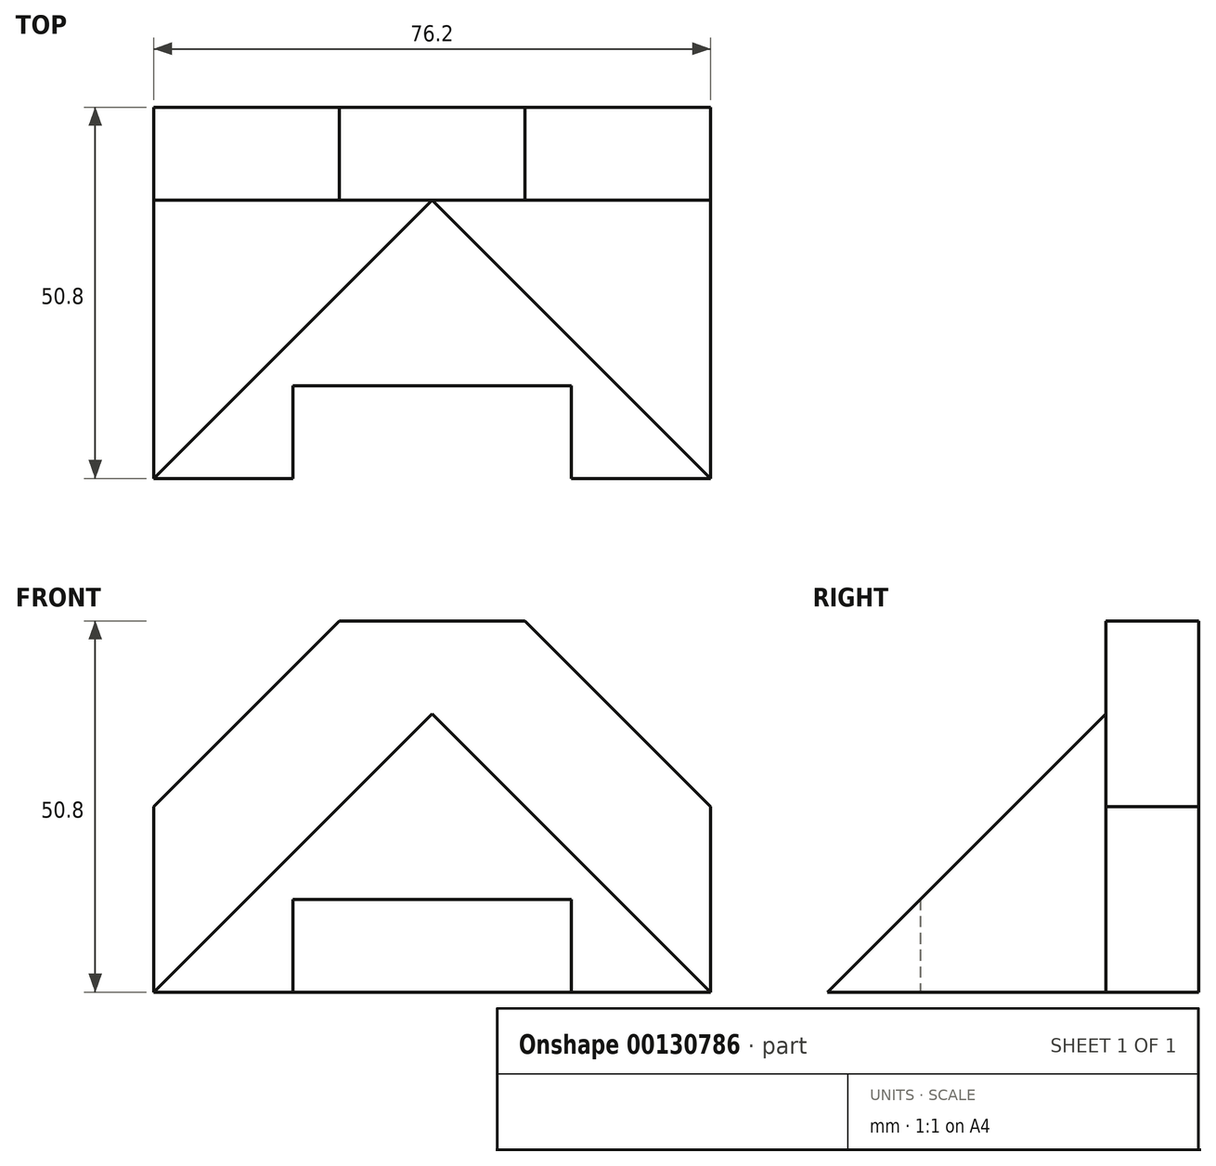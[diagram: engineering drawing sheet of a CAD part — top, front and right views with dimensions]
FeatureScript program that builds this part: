
annotation { "Feature Type Name" : "Feature", "Feature Type Description" : "" }
export const myFeature = defineFeature(function(context is Context, id is Id, definition is map)
    precondition{}
    {
        {
            var Q0;
            Q0=qCreatedBy(makeId("Front.planeOp"),FACE);
            var sketch = newSketch(context, id + "F0", { "sketchPlane" : qUnion([Q0])});
            skLineSegment(sketch, "E0", {"start": v(0, 0) * mm, "end": v(0, 25.4) * mm});
            skLineSegment(sketch, "E1", {"start": v(0, 25.4) * mm, "end": v(25.4, 50.8) * mm});
            skLineSegment(sketch, "E2", {"start": v(25.4, 50.8) * mm, "end": v(50.8, 50.8) * mm});
            skLineSegment(sketch, "E3", {"start": v(50.8, 50.8) * mm, "end": v(76.2, 25.4) * mm});
            skLineSegment(sketch, "E4", {"start": v(76.2, 25.4) * mm, "end": v(76.2, 0) * mm});
            skLineSegment(sketch, "E5", {"start": v(76.2, 0) * mm, "end": v(0, 0) * mm});
            skSolve(sketch);
        }
        {
            var Q0;
            Q0 = qSketchRegion(id + "F0", true);
            extrude(context, id + "F1", {"entities" : qUnion([Q0]), "depth" : 12.7 * mm});
        }
        {
            var Q0;
            Q0=makeQuery(id+"F1.opExtrude","CAP_FACE",FACE,{"disambiguationData":[OSD([sQuery(id+"F0.wireOp",EDGE,"E0"),sQuery(id+"F0.wireOp",EDGE,"E1"),sQuery(id+"F0.wireOp",EDGE,"E2"),sQuery(id+"F0.wireOp",EDGE,"E3"),sQuery(id+"F0.wireOp",EDGE,"E4"),sQuery(id+"F0.wireOp",EDGE,"E5")])],"isStart":false});
            var sketch = newSketch(context, id + "F2", { "sketchPlane" : qUnion([Q0])});
            skLineSegment(sketch, "E6", {"start": v(0, 0) * mm, "end": v(38.1, 38.1) * mm});
            skLineSegment(sketch, "E7", {"start": v(38.1, 38.1) * mm, "end": v(76.2, 0) * mm});
            skLineSegment(sketch, "E8", {"start": v(76.2, 0) * mm, "end": v(0, 0) * mm});
            skSolve(sketch);
        }
        {
            var Q0;
            Q0=makeQuery(id+"F2.imprint","IMPRINT",FACE,{"disambiguationData":[TD([[makeQuery(id+"F2.imprint","IMPRINT",EDGE,{"derivedFrom":sQuery(id+"F2.wireOp",EDGE,"E6")}),-1.0]])]});
            extrude(context, id + "F3", {"entities" : qUnion([Q0]), "operationType" : NewBodyOperationType.ADD, "depth" : 38.1 * mm});
        }
        {
            var Q0;
            Q0=makeQuery(id+"F3.opExtrude","CAP_FACE",FACE,{"disambiguationData":[OSD([sQuery(id+"F2.wireOp",EDGE,"E6"),sQuery(id+"F2.wireOp",EDGE,"E7"),sQuery(id+"F2.wireOp",EDGE,"E8")])],"isStart":false});
            var sketch = newSketch(context, id + "F4", { "sketchPlane" : qUnion([Q0])});
            skLineSegment(sketch, "E9.bottom", {"start": v(19.05, 12.7) * mm, "end": v(57.15, 12.7) * mm});
            skLineSegment(sketch, "E9.top", {"start": v(19.05, 0) * mm, "end": v(57.15, 0) * mm});
            skLineSegment(sketch, "E9.left", {"start": v(19.05, 12.7) * mm, "end": v(19.05, 0) * mm});
            skLineSegment(sketch, "E9.right", {"start": v(57.15, 12.7) * mm, "end": v(57.15, 0) * mm});
            skSolve(sketch);
        }
        {
            var Q0;
            Q0=makeQuery(id+"F4.imprint","IMPRINT",FACE,{"disambiguationData":[TD([[makeQuery(id+"F4.imprint","IMPRINT",EDGE,{"derivedFrom":sQuery(id+"F4.wireOp",EDGE,"E9.bottom")}),-1.0]])]});
            extrude(context, id + "F5", {"entities" : qUnion([Q0]), "operationType" : NewBodyOperationType.REMOVE, "oppositeDirection" : true, "depth" : 12.7 * mm});
        }
        {
            var Q0;
            Q0=makeQuery(id+"F1.opExtrude","SWEPT_FACE",FACE,{"disambiguationData":[OSD([sQuery(id+"F0.wireOp",EDGE,"E4")])]});
            var sketch = newSketch(context, id + "F6", { "sketchPlane" : qUnion([Q0])});
            skLineSegment(sketch, "E10.0", {"start": v(-50.8, 38.1) * mm, "end": v(-12.7, 38.1) * mm});
            skLineSegment(sketch, "E11.0", {"start": v(-12.7, 50.8) * mm, "end": v(-12.7, 25.4) * mm});
            skLineSegment(sketch, "E12.0", {"start": v(-50.8, 38.1) * mm, "end": v(-50.8, 0) * mm});
            skLineSegment(sketch, "E13.0", {"start": v(-50.8, 0) * mm, "end": v(-12.7, 0) * mm});
            skLineSegment(sketch, "E14", {"start": v(-50.8, 0) * mm, "end": v(-12.7, 38.1) * mm});
            skLineSegment(sketch, "E15", {"start": v(-12.7, 0) * mm, "end": v(-50.8, 0) * mm});
            skSolve(sketch);
        }
        {
            var Q0;
            Q0=makeQuery(id+"F6.imprint","IMPRINT",FACE,{"disambiguationData":[TD([[makeQuery(id+"F6.imprint","IMPRINT",EDGE,{"derivedFrom":sQuery(id+"F6.wireOp",EDGE,"E10.0")}),-1.0]])]});
            extrude(context, id + "F7", {"entities" : qUnion([Q0]), "operationType" : NewBodyOperationType.REMOVE, "endBound" : BoundingType.THROUGH_ALL, "oppositeDirection" : true, "depth" : 25.4 * mm});
        }
    });
